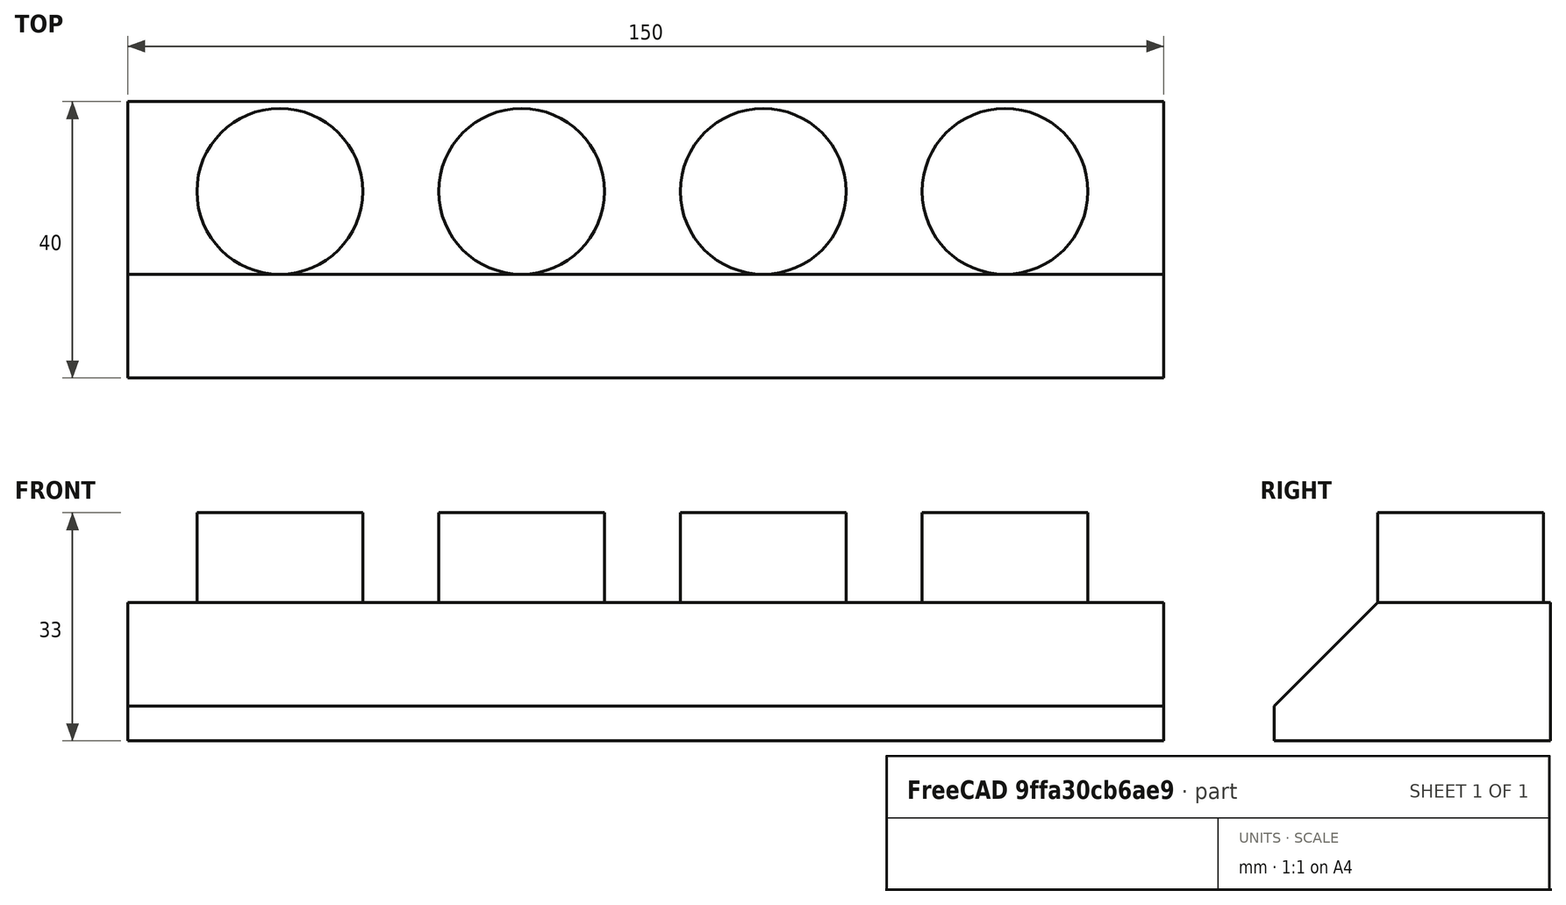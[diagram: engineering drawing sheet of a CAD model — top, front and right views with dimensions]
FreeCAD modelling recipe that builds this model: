
FCSTD DOCUMENT  (FreeCAD 0.14R2935 (Git))
Label: soporte-rasquetas
License: CC-BY 3.0
LicenseURL: http://creativecommons.org/licenses/by/3.0/
objects: Part::Cylinder×1, Part::FeaturePython×1, Part::Box×1, Part::MultiFuse×1, PartDesign::Chamfer×1
note: 5 computed .brp shape members not serialized (recipe doc carries the construction recipe); baked Part::Feature solids carry a one-line shape summary decoded from their .brp

FEATURE [Part::Cylinder] Cylinder
  Angle = 360
  Height = 15
  Radius = 12
FEATURE [Part::FeaturePython] Array  # Draft array (typed FeaturePython)
  Angle = 360
  ArrayType = 0
  Axis = (0,0,1)
  Base = -> Cylinder
  Center = (0,0,0)
  IntervalX = (35,0,0)
  IntervalY = (0,1,0)
  IntervalZ = (0,0,1)
  NumberPolar = 1
  NumberX = 4
  NumberY = 1
  NumberZ = 1
FEATURE [Part::Box] Box
  Height = 20
  Length = 150
  Placement = pos=(-22,-27,-18) rot=(0,0,1;0rad)
  Width = 40
FEATURE [Part::MultiFuse] Fusion
  Shapes = -> [Box,Array]
FEATURE [PartDesign::Chamfer] Chamfer
  Base = -> Fusion [Edge7]
  Size = 15
